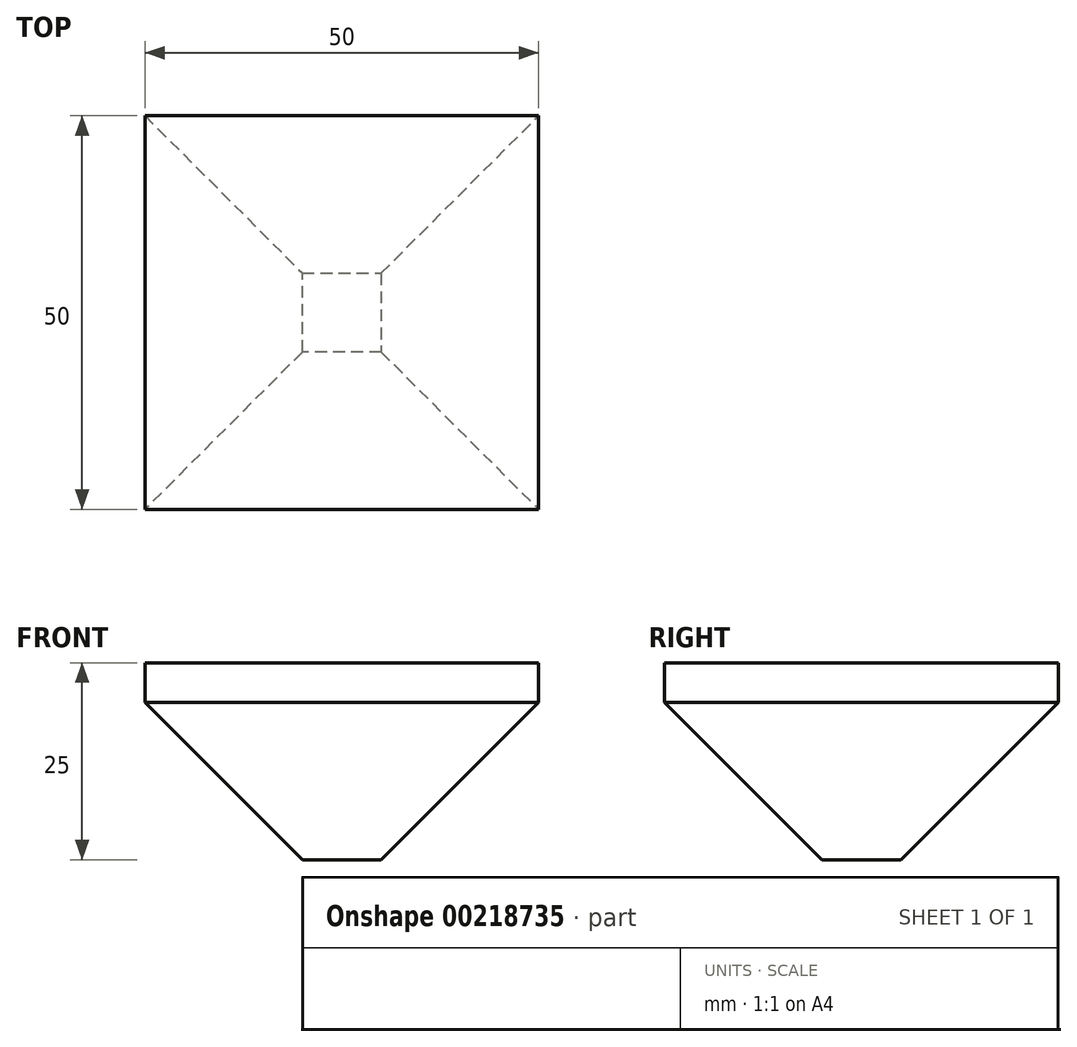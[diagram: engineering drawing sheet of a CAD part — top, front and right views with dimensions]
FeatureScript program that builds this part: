
annotation { "Feature Type Name" : "Feature", "Feature Type Description" : "" }
export const myFeature = defineFeature(function(context is Context, id is Id, definition is map)
    precondition{}
    {
        {
            var Q0;
            Q0=qCreatedBy(makeId("Top.planeOp"),FACE);
            var sketch = newSketch(context, id + "F0", { "sketchPlane" : qUnion([Q0])});
            skLineSegment(sketch, "E0.bottom", {"start": v(0, 50) * mm, "end": v(50, 50) * mm});
            skLineSegment(sketch, "E0.top", {"start": v(0, 0) * mm, "end": v(50, 0) * mm});
            skLineSegment(sketch, "E0.left", {"start": v(0, 50) * mm, "end": v(0, 0) * mm});
            skLineSegment(sketch, "E0.right", {"start": v(50, 50) * mm, "end": v(50, 0) * mm});
            skSolve(sketch);
        }
        {
            var Q0;
            Q0=makeQuery(id+"F0.imprint","IMPRINT",FACE,{"disambiguationData":[TD([[makeQuery(id+"F0.imprint","IMPRINT",EDGE,{"derivedFrom":sQuery(id+"F0.wireOp",EDGE,"E0.bottom")}),-1.0]])]});
            extrude(context, id + "F1", {"entities" : qUnion([Q0]), "depth" : 25 * mm});
        }
        {
            var Q0;
            Q0=makeQuery(id+"F1.opExtrude","CAP_EDGE",EDGE,{"disambiguationData":[OSD([sQuery(id+"F0.wireOp",EDGE,"E0.top")])],"isStart":true});
            var Q1;
            Q1=makeQuery(id+"F1.opExtrude","CAP_EDGE",EDGE,{"disambiguationData":[OSD([sQuery(id+"F0.wireOp",EDGE,"E0.bottom")])],"isStart":true});
            var Q2;
            Q2=makeQuery(id+"F1.opExtrude","CAP_EDGE",EDGE,{"disambiguationData":[OSD([sQuery(id+"F0.wireOp",EDGE,"E0.left")])],"isStart":true});
            var Q3;
            Q3=makeQuery(id+"F1.opExtrude","CAP_EDGE",EDGE,{"disambiguationData":[OSD([sQuery(id+"F0.wireOp",EDGE,"E0.right")])],"isStart":true});
            chamfer(context, id + "F2", {"entities" : qUnion([Q0, Q1, Q2, Q3]), "width" : 20 * mm, "tangentPropagation" : true});
        }
    });
